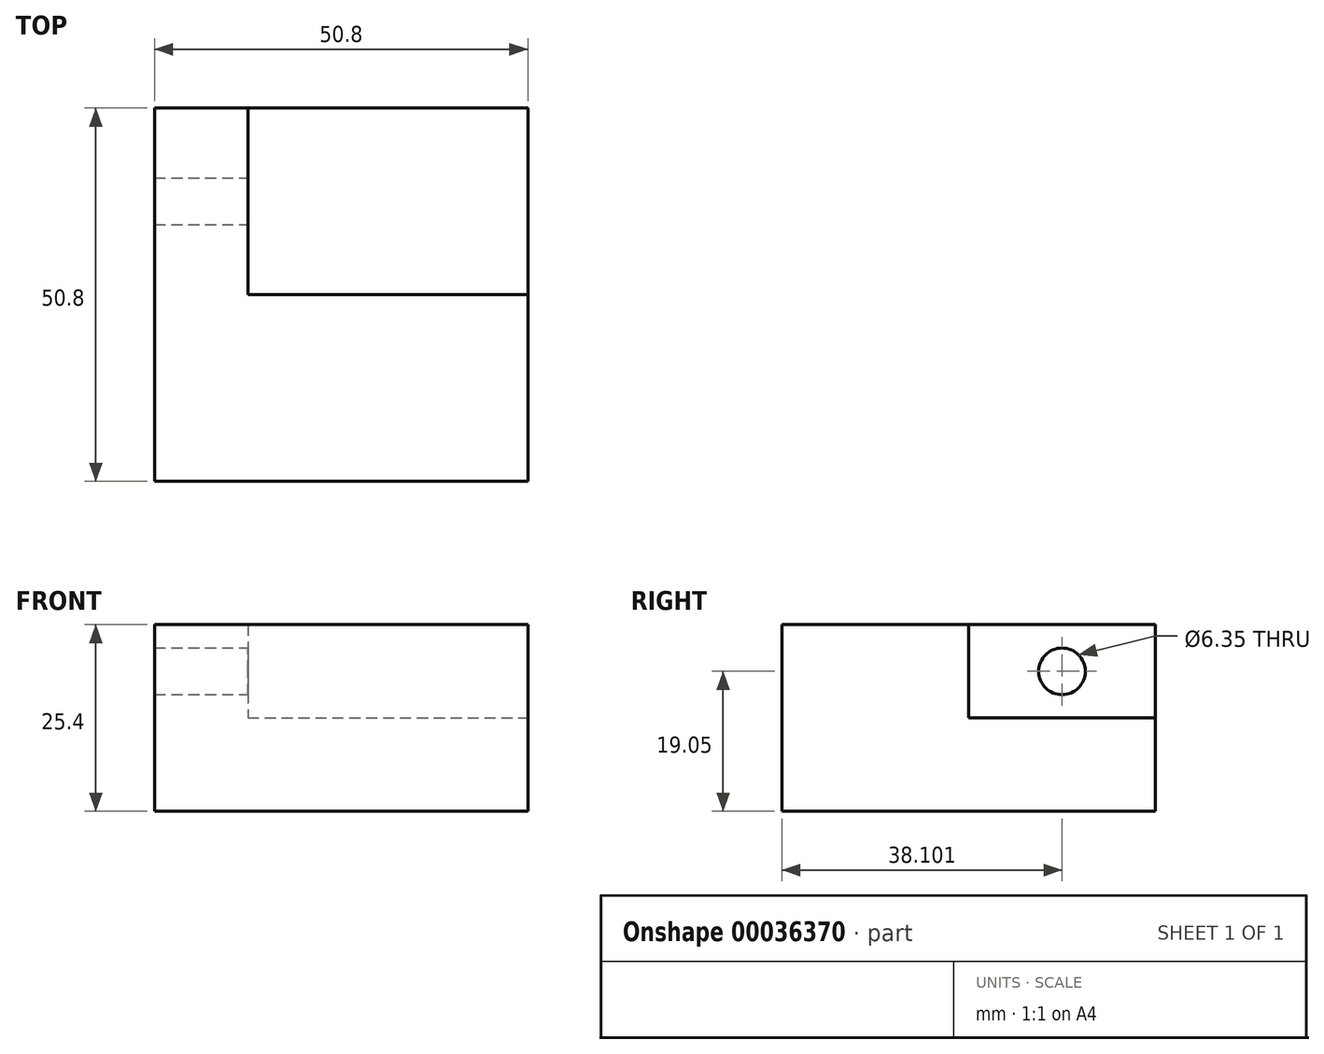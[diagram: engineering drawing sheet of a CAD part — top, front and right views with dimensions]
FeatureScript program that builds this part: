
annotation { "Feature Type Name" : "Feature", "Feature Type Description" : "" }
export const myFeature = defineFeature(function(context is Context, id is Id, definition is map)
    precondition{}
    {
        {
            var Q0;
            Q0=qCreatedBy(makeId("Top.planeOp"),FACE);
            var sketch = newSketch(context, id + "F0", { "sketchPlane" : qUnion([Q0])});
            skLineSegment(sketch, "E0", {"start": v(31.63, 59.4) * mm, "end": v(-19.17, 59.4) * mm});
            skLineSegment(sketch, "E1", {"start": v(31.63, 59.4) * mm, "end": v(31.63, 8.6) * mm});
            skLineSegment(sketch, "E2", {"start": v(-19.17, 59.4) * mm, "end": v(-19.17, 8.6) * mm});
            skLineSegment(sketch, "E3", {"start": v(31.63, 8.6) * mm, "end": v(-19.17, 8.6) * mm});
            skSolve(sketch);
        }
        {
            var Q0;
            Q0=makeQuery(id+"F0.imprint","IMPRINT",FACE,{"disambiguationData":[TD([[makeQuery(id+"F0.imprint","IMPRINT",EDGE,{"derivedFrom":sQuery(id+"F0.wireOp",EDGE,"E0")}),1.0]])]});
            extrude(context, id + "F1", {"entities" : qUnion([Q0]), "endBound" : BoundingType.SYMMETRIC, "depth" : 12.7 * mm});
        }
        {
            var Q0;
            Q0=makeQuery(id+"F1.opExtrude","CAP_FACE",FACE,{"disambiguationData":[OSD([sQuery(id+"F0.wireOp",EDGE,"E0"),sQuery(id+"F0.wireOp",EDGE,"E1"),sQuery(id+"F0.wireOp",EDGE,"E2"),sQuery(id+"F0.wireOp",EDGE,"E3")])],"isStart":false});
            var sketch = newSketch(context, id + "F2", { "sketchPlane" : qUnion([Q0])});
            skLineSegment(sketch, "E4.bottom", {"start": v(31.63, 8.6) * mm, "end": v(-19.17, 8.6) * mm});
            skLineSegment(sketch, "E4.top", {"start": v(31.63, 34) * mm, "end": v(-19.17, 34) * mm});
            skLineSegment(sketch, "E4.left", {"start": v(31.63, 8.6) * mm, "end": v(31.63, 34) * mm});
            skLineSegment(sketch, "E4.right", {"start": v(-19.17, 8.6) * mm, "end": v(-19.17, 34) * mm});
            skSolve(sketch);
        }
        {
            var Q0;
            Q0=makeQuery(id+"F2.imprint","IMPRINT",FACE,{"disambiguationData":[TD([[makeQuery(id+"F2.imprint","IMPRINT",EDGE,{"derivedFrom":sQuery(id+"F2.wireOp",EDGE,"E4.bottom")}),-1.0]])]});
            extrude(context, id + "F3", {"entities" : qUnion([Q0]), "operationType" : NewBodyOperationType.ADD, "endBound" : BoundingType.SYMMETRIC, "depth" : 25.4 * mm});
        }
        {
            var Q0;
            Q0=makeQuery(id+"F1.opExtrude","CAP_FACE",FACE,{"disambiguationData":[OSD([sQuery(id+"F0.wireOp",EDGE,"E0"),sQuery(id+"F0.wireOp",EDGE,"E1"),sQuery(id+"F0.wireOp",EDGE,"E2"),sQuery(id+"F0.wireOp",EDGE,"E3")])],"isStart":false});
            var sketch = newSketch(context, id + "F4", { "sketchPlane" : qUnion([Q0])});
            skLineSegment(sketch, "E5", {"start": v(-19.17, 34) * mm, "end": v(-19.17, 59.4) * mm});
            skLineSegment(sketch, "E6", {"start": v(-19.17, 59.4) * mm, "end": v(-6.47, 59.4) * mm});
            skLineSegment(sketch, "E7", {"start": v(-6.47, 59.4) * mm, "end": v(-6.47, 34) * mm});
            skLineSegment(sketch, "E8", {"start": v(-19.17, 34) * mm, "end": v(-6.47, 34) * mm});
            skSolve(sketch);
        }
        {
            var Q0;
            Q0=makeQuery(id+"F4.imprint","IMPRINT",FACE,{"disambiguationData":[TD([[makeQuery(id+"F4.imprint","IMPRINT",EDGE,{"derivedFrom":sQuery(id+"F4.wireOp",EDGE,"E5")}),1.0]])]});
            extrude(context, id + "F5", {"entities" : qUnion([Q0]), "operationType" : NewBodyOperationType.ADD, "endBound" : BoundingType.SYMMETRIC, "depth" : 25.4 * mm});
        }
        {
            var Q0;
            Q0=makeQuery(id+"F5.opExtrude","SWEPT_FACE",FACE,{"disambiguationData":[OSD([sQuery(id+"F4.wireOp",EDGE,"E7")])]});
            var sketch = newSketch(context, id + "F6", { "sketchPlane" : qUnion([Q0])});
            skLineSegment(sketch, "E9", {"start": v(46.7, 6.35) * mm, "end": v(46.7, 12.7) * mm});
            skCircle(sketch, "E10", {"center": v(46.7, 12.7) * mm, "radius": 3.57 * mm});
            skSolve(sketch);
        }
        {
            var Q0;
            Q0=sQuery(id+"F6.wireOp",VERTEX,"E10.center");
            var Q1;
            Q1=makeQuery(id+"F1.opExtrude","SWEPT_BODY",BODY,{"disambiguationData":[OSD([sQuery(id+"F0.wireOp",EDGE,"E0"),sQuery(id+"F0.wireOp",EDGE,"E1"),sQuery(id+"F0.wireOp",EDGE,"E2"),sQuery(id+"F0.wireOp",EDGE,"E3")])]});
            hole(context, id + "F7", {"style" : HoleStyle.SIMPLE, "holeDiameter" : 6.35 * mm, "endStyle" : HoleEndStyle.THROUGH, "locations" : qUnion([Q0]), "scope" : qUnion([Q1])});
        }
    });
